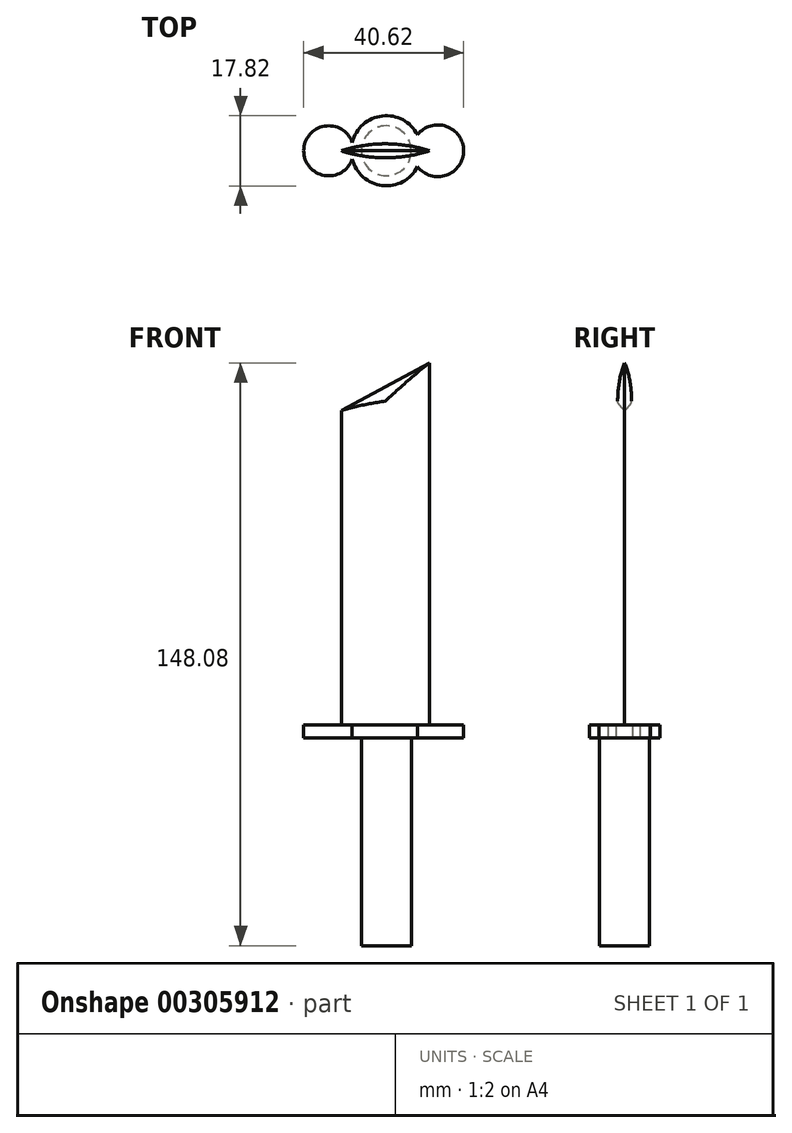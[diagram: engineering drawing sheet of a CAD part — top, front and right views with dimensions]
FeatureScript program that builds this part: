
annotation { "Feature Type Name" : "Feature", "Feature Type Description" : "" }
export const myFeature = defineFeature(function(context is Context, id is Id, definition is map)
    precondition{}
    {
        {
            var Q0;
            Q0=qCreatedBy(makeId("Front.planeOp"),FACE);
            var sketch = newSketch(context, id + "F0", { "sketchPlane" : qUnion([Q0])});
            skLineSegment(sketch, "E0", {"start": v(-24.48, -21.71) * mm, "end": v(-2.13, -21.71) * mm});
            skLineSegment(sketch, "E1", {"start": v(-2.13, -21.71) * mm, "end": v(-2.13, 66.55) * mm});
            skLineSegment(sketch, "E2", {"start": v(-24.48, -21.71) * mm, "end": v(-24.48, 54.49) * mm});
            skLineSegment(sketch, "E3", {"start": v(-24.48, 54.49) * mm, "end": v(-2.13, 66.55) * mm});
            skPoint(sketch, "E4", {"position": v(-26.52, -21.6) * mm});
            skSolve(sketch);
        }
        {
            var Q0;
            Q0=makeQuery(id+"F0.imprint","IMPRINT",FACE,{"disambiguationData":[TD([[makeQuery(id+"F0.imprint","IMPRINT",EDGE,{"derivedFrom":sQuery(id+"F0.wireOp",EDGE,"E0")}),1.0]])]});
            extrude(context, id + "F1", {"entities" : qUnion([Q0]), "depth" : 1.78 * mm});
        }
        {
            var Q0;
            Q0=makeQuery(id+"F3.opFillet","BLEND_EDGE",EDGE,{"blendedFrom":[makeQuery(id+"F1.opExtrude","CAP_EDGE",EDGE,{"disambiguationData":[OSD([sQuery(id+"F0.wireOp",EDGE,"E2")])],"isStart":false}),makeQuery(id+"F1.opExtrude","SWEPT_FACE",FACE,{"disambiguationData":[OSD([sQuery(id+"F0.wireOp",EDGE,"E3")])]})],"blendedInto":[makeQuery(id+"F1.opExtrude","SWEPT_FACE",FACE,{"disambiguationData":[OSD([sQuery(id+"F0.wireOp",EDGE,"E3")])]})]});
            var Q1;
            Q1=makeQuery(id+"F1.opExtrude","CAP_EDGE",EDGE,{"disambiguationData":[OSD([sQuery(id+"F0.wireOp",EDGE,"E3")])],"isStart":false});
            fillet(context, id + "F2", {"entities" : qUnion([Q0, Q1]), "radius" : 3.8 * mm, "tangentPropagation" : true, "allowEdgeOverflow" : false});
        }
        {
            var Q0;
            Q0=makeQuery(id+"F1.opExtrude","CAP_EDGE",EDGE,{"disambiguationData":[OSD([sQuery(id+"F0.wireOp",EDGE,"E2")])],"isStart":false});
            var Q1;
            Q1=makeQuery(id+"F1.opExtrude","CAP_EDGE",EDGE,{"disambiguationData":[OSD([sQuery(id+"F0.wireOp",EDGE,"E1")])],"isStart":false});
            fillet(context, id + "F3", {"entities" : qUnion([Q0, Q1]), "radius" : 36.83 * mm, "tangentPropagation" : true, "allowEdgeOverflow" : false});
        }
        {
            var Q0;
            Q0=makeQuery(id+"F1.opExtrude","SWEPT_BODY",BODY,{"disambiguationData":[OSD([sQuery(id+"F0.wireOp",EDGE,"E0"),sQuery(id+"F0.wireOp",EDGE,"E1"),sQuery(id+"F0.wireOp",EDGE,"E2"),sQuery(id+"F0.wireOp",EDGE,"E3")])]});
            var Q1;
            Q1=makeQuery(id+"F1.opExtrude","CAP_FACE",FACE,{"disambiguationData":[OSD([sQuery(id+"F0.wireOp",EDGE,"E0"),sQuery(id+"F0.wireOp",EDGE,"E1"),sQuery(id+"F0.wireOp",EDGE,"E2"),sQuery(id+"F0.wireOp",EDGE,"E3")])],"isStart":true});
            mirror(context, id + "F4", {"operationType" : NewBodyOperationType.ADD, "entities" : qUnion([Q0]), "mirrorPlane" : qUnion([Q1])});
        }
        {
            var Q0;
            Q0=qCreatedBy(makeId("Top.planeOp"),FACE);
            var sketch = newSketch(context, id + "F5", { "sketchPlane" : qUnion([Q0])});
            skCircle(sketch, "E5", {"center": v(-27.7, 0) * mm, "radius": 6.35 * mm});
            skCircle(sketch, "E6", {"center": v(-13.07, 0) * mm, "radius": 8.9 * mm});
            skCircle(sketch, "E7", {"center": v(0, 0) * mm, "radius": 6.57 * mm});
            skCircle(sketch, "E8", {"center": v(-13.07, 0) * mm, "radius": 6.35 * mm});
            skSolve(sketch);
        }
        {
            var Q0;
            Q0 = qSketchRegion(id + "F5", true);
            var Q1;
            Q1=makeQuery(id+"F5.imprint","IMPRINT",FACE,{"disambiguationData":[TD([[makeQuery(id+"F5.imprint","IMPRINT",EDGE,{"derivedFrom":sQuery(id+"F5.wireOp",EDGE,"E8")}),1.0]])]});
            extrude(context, id + "F6", {"entities" : qUnion([Q0, Q1]), "operationType" : NewBodyOperationType.ADD, "oppositeDirection" : true, "depth" : 28.7 * mm});
        }
        {
            var Q0;
            Q0=makeQuery(id+"F6.opExtrude","CAP_FACE",FACE,{"disambiguationData":[OSD([sQuery(id+"F5.wireOp",EDGE,"E5"),sQuery(id+"F5.wireOp",EDGE,"E6"),sQuery(id+"F5.wireOp",EDGE,"E7")])],"isStart":true});
            extrude(context, id + "F7", {"entities" : qUnion([Q0]), "operationType" : NewBodyOperationType.REMOVE, "oppositeDirection" : true, "depth" : 25.4 * mm});
        }
        {
            var Q0;
            Q0=makeQuery(id+"F5.imprint","IMPRINT",FACE,{"disambiguationData":[TD([[makeQuery(id+"F5.imprint","IMPRINT",EDGE,{"derivedFrom":sQuery(id+"F5.wireOp",EDGE,"E8")}),1.0]])]});
            extrude(context, id + "F8", {"entities" : qUnion([Q0]), "operationType" : NewBodyOperationType.ADD, "oppositeDirection" : true, "depth" : 81.53 * mm});
        }
        {
            var Q0;
            {var subQ6=sQuery(id+"F0.wireOp",EDGE,"E1");var subQ7=makeQuery(id+"F3.opFillet","BLEND_FACE",FACE,{"disambiguationData":[OSD([subQ6])]});var subQ8=sQuery(id+"F5.wireOp",EDGE,"E8");Q0=makeQuery(id+"F8.boolean.opBoolean","SPLIT",FACE,{"disambiguationData":[TD([subQ7])],"derivedFrom":makeQuery(id+"F8.opExtrude","CAP_FACE",FACE,{"disambiguationData":[OSD([subQ8])],"isStart":true})});}
            var Q1;
            {var subQ6=sQuery(id+"F0.wireOp",EDGE,"E1");var subQ7=makeQuery(id+"F4.opPattern","COPY",FACE,{"derivedFrom":makeQuery(id+"F3.opFillet","BLEND_FACE",FACE,{"disambiguationData":[OSD([subQ6])]}),"instanceName":"1"});var subQ8=sQuery(id+"F5.wireOp",EDGE,"E8");Q1=makeQuery(id+"F8.boolean.opBoolean","SPLIT",FACE,{"disambiguationData":[TD([subQ7])],"derivedFrom":makeQuery(id+"F8.opExtrude","CAP_FACE",FACE,{"disambiguationData":[OSD([subQ8])],"isStart":true})});}
            extrude(context, id + "F9", {"entities" : qUnion([Q0, Q1]), "operationType" : NewBodyOperationType.REMOVE, "oppositeDirection" : true, "depth" : 25.4 * mm});
        }
    });
